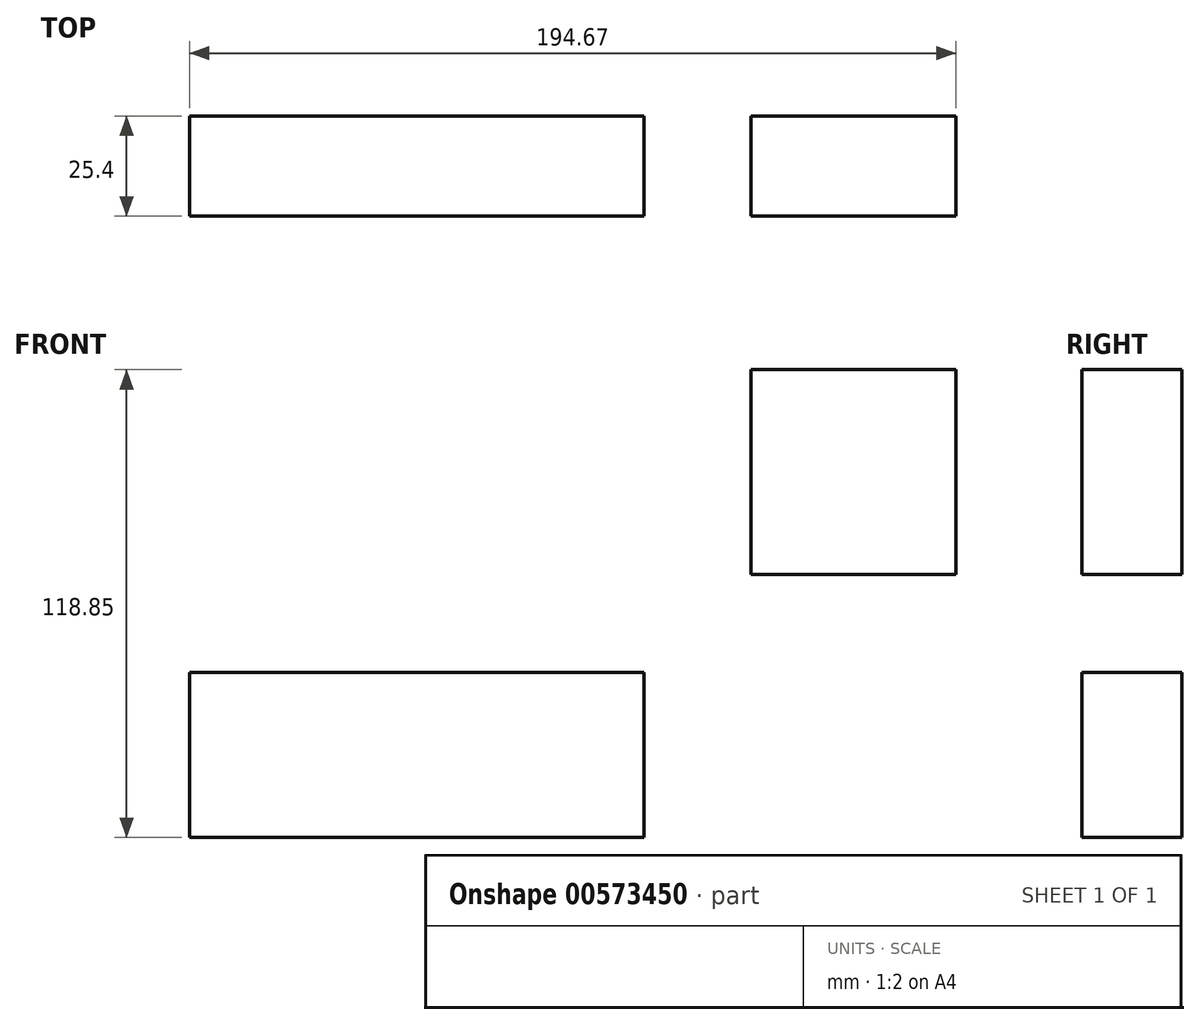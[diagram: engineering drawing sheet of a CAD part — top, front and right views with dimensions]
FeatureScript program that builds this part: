
annotation { "Feature Type Name" : "Feature", "Feature Type Description" : "" }
export const myFeature = defineFeature(function(context is Context, id is Id, definition is map)
    precondition{}
    {
        {
            var Q0;
            Q0=qCreatedBy(makeId("Front.planeOp"),FACE);
            var sketch = newSketch(context, id + "F0", { "sketchPlane" : qUnion([Q0])});
            skLineSegment(sketch, "E0.bottom", {"start": v(57.72, -20.94) * mm, "end": v(-57.72, -20.94) * mm});
            skLineSegment(sketch, "E0.top", {"start": v(57.72, 20.94) * mm, "end": v(-57.72, 20.94) * mm});
            skLineSegment(sketch, "E0.left", {"start": v(57.72, -20.94) * mm, "end": v(57.72, 20.94) * mm});
            skLineSegment(sketch, "E0.right", {"start": v(-57.72, -20.94) * mm, "end": v(-57.72, 20.94) * mm});
            skPoint(sketch, "E0.middle", {"position": v(0, 0) * mm});
            skLineSegment(sketch, "E1.bottom", {"start": v(84.89, 45.84) * mm, "end": v(136.95, 45.84) * mm});
            skLineSegment(sketch, "E1.top", {"start": v(84.89, 97.9) * mm, "end": v(136.95, 97.9) * mm});
            skLineSegment(sketch, "E1.left", {"start": v(84.89, 45.84) * mm, "end": v(84.89, 97.9) * mm});
            skLineSegment(sketch, "E1.right", {"start": v(136.95, 45.84) * mm, "end": v(136.95, 97.9) * mm});
            skPoint(sketch, "E1.middle", {"position": v(110.92, 71.87) * mm});
            skLineSegment(sketch, "E2.bottom", {"start": v(57.72, 45.84) * mm, "end": v(57.72, 45.84) * mm});
            skLineSegment(sketch, "E2.top", {"start": v(57.72, -3.96) * mm, "end": v(57.72, -3.96) * mm});
            skLineSegment(sketch, "E2.left", {"start": v(57.72, 45.84) * mm, "end": v(57.72, -3.96) * mm});
            skLineSegment(sketch, "E2.right", {"start": v(57.72, 45.84) * mm, "end": v(57.72, -3.96) * mm});
            skPoint(sketch, "E2.middle", {"position": v(57.72, 20.94) * mm});
            skArc(sketch, "E3", {"start": v(57.72, 45.84) * mm, "mid": v(62.37, 57.05) * mm, "end": v(73.57, 61.69) * mm});
            skLineSegment(sketch, "E4", {"start": v(73.57, 61.69) * mm, "end": v(103, 61.69) * mm});
            skSolve(sketch);
        }
        {
            var Q0;
            Q0 = qSketchRegion(id + "F0", true);
            extrude(context, id + "F1", {"entities" : qUnion([Q0]), "depth" : 25.4 * mm, "offsetDistance" : 25.4 * mm});
        }
    });
